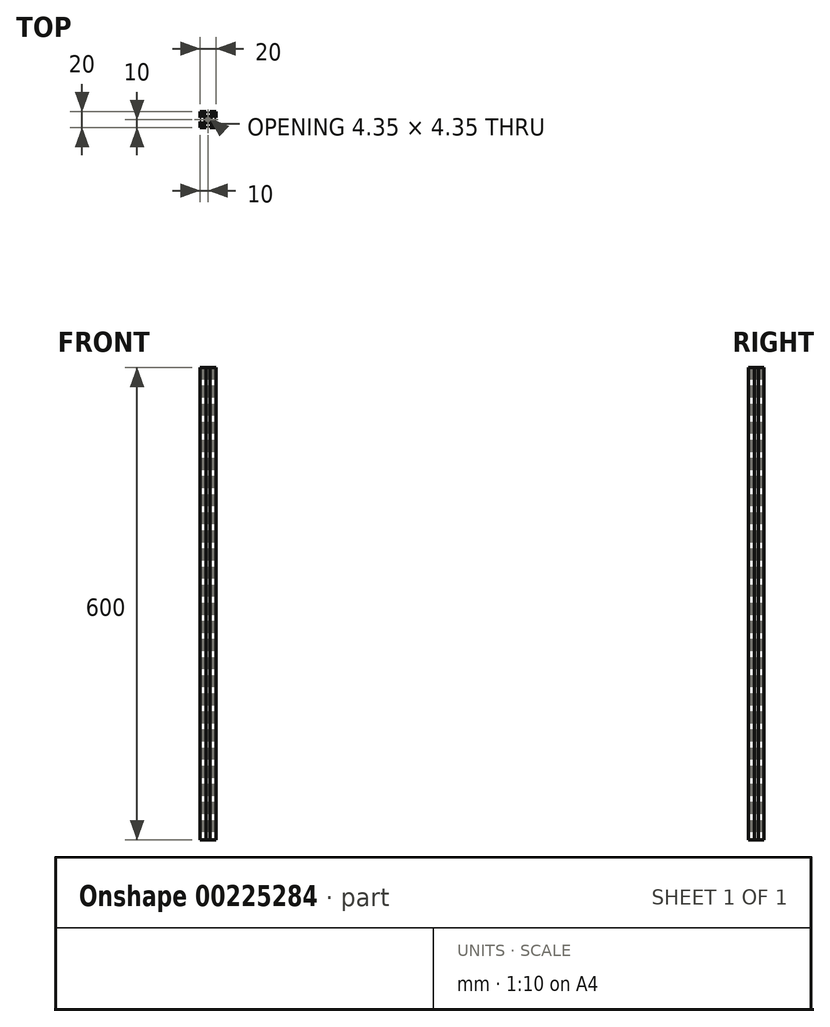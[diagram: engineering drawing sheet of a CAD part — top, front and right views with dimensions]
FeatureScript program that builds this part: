
annotation { "Feature Type Name" : "Feature", "Feature Type Description" : "" }
export const myFeature = defineFeature(function(context is Context, id is Id, definition is map)
    precondition{}
    {
        {
            var Q0;
            Q0=qCreatedBy(makeId("Top.planeOp"),FACE);
            var sketch = newSketch(context, id + "F0", { "sketchPlane" : qUnion([Q0])});
            skLineSegment(sketch, "E0.bottom", {"start": v(10, 10) * mm, "end": v(-10, 10) * mm});
            skLineSegment(sketch, "E0.top", {"start": v(10, -10) * mm, "end": v(-10, -10) * mm});
            skLineSegment(sketch, "E0.left", {"start": v(10, 10) * mm, "end": v(10, -10) * mm});
            skLineSegment(sketch, "E0.right", {"start": v(-10, 10) * mm, "end": v(-10, -10) * mm});
            skPoint(sketch, "E0.middle", {"position": v(0, 0) * mm});
            skLineSegment(sketch, "E1", {"start": v(-10, 10) * mm, "end": v(10, -10) * mm, "construction": true});
            skLineSegment(sketch, "E2", {"start": v(-10, -10) * mm, "end": v(10, 10) * mm, "construction": true});
            skLineSegment(sketch, "E3", {"start": v(0, 10) * mm, "end": v(0, -10) * mm, "construction": true});
            skLineSegment(sketch, "E4", {"start": v(-10, 0) * mm, "end": v(10, 0) * mm, "construction": true});
            skPoint(sketch, "E4.endSnap0", {"position": v(10, 0) * mm});
            skLineSegment(sketch, "E5", {"start": v(-2.63, 13.49) * mm, "end": v(2.63, 13.49) * mm});
            skLineSegment(sketch, "E6", {"start": v(2.63, 13.49) * mm, "end": v(2.63, 8.5) * mm});
            skLineSegment(sketch, "E7", {"start": v(2.63, 8.5) * mm, "end": v(6, 8.5) * mm});
            skLineSegment(sketch, "E8", {"start": v(6, 8.5) * mm, "end": v(6, 7.06) * mm});
            skLineSegment(sketch, "E9", {"start": v(6, 7.06) * mm, "end": v(2.6, 3.66) * mm});
            skLineSegment(sketch, "E10", {"start": v(2.6, 3.66) * mm, "end": v(-2.6, 3.66) * mm});
            skLineSegment(sketch, "E11", {"start": v(-2.6, 3.66) * mm, "end": v(-6, 7.06) * mm});
            skLineSegment(sketch, "E12", {"start": v(-6, 7.06) * mm, "end": v(-6, 8.5) * mm});
            skLineSegment(sketch, "E13", {"start": v(-6, 8.5) * mm, "end": v(-2.63, 8.5) * mm});
            skLineSegment(sketch, "E14", {"start": v(-2.63, 8.5) * mm, "end": v(-2.63, 13.49) * mm});
            skCircle(sketch, "E15", {"center": v(0, 0) * mm, "radius": 2.1 * mm});
            skLineSegment(sketch, "E16.MirrorCS", {"start": v(-7.06, 6) * mm, "end": v(-8.5, 6) * mm});
            skLineSegment(sketch, "E17.MirrorCS", {"start": v(-3.66, 2.6) * mm, "end": v(-7.06, 6) * mm});
            skLineSegment(sketch, "E18.MirrorCS", {"start": v(-8.5, 6) * mm, "end": v(-8.5, 2.63) * mm});
            skLineSegment(sketch, "E19.MirrorCS", {"start": v(-3.66, -2.6) * mm, "end": v(-3.66, 2.6) * mm});
            skLineSegment(sketch, "E20.MirrorCS", {"start": v(-7.06, -6) * mm, "end": v(-3.66, -2.6) * mm});
            skLineSegment(sketch, "E21.MirrorCS", {"start": v(-8.5, -6) * mm, "end": v(-7.06, -6) * mm});
            skLineSegment(sketch, "E22.MirrorCS", {"start": v(-8.5, -2.63) * mm, "end": v(-8.5, -6) * mm});
            skLineSegment(sketch, "E23.MirrorCS", {"start": v(-13.49, -2.63) * mm, "end": v(-8.5, -2.63) * mm});
            skLineSegment(sketch, "E24.MirrorCS", {"start": v(-13.49, 2.63) * mm, "end": v(-13.49, -2.63) * mm});
            skLineSegment(sketch, "E25.MirrorCS", {"start": v(-8.5, 2.63) * mm, "end": v(-13.49, 2.63) * mm});
            skLineSegment(sketch, "E26.MirrorCS", {"start": v(-2.6, -3.66) * mm, "end": v(-6, -7.06) * mm});
            skLineSegment(sketch, "E27.MirrorCS", {"start": v(2.6, -3.66) * mm, "end": v(-2.6, -3.66) * mm});
            skLineSegment(sketch, "E28.MirrorCS", {"start": v(6, -7.06) * mm, "end": v(2.6, -3.66) * mm});
            skLineSegment(sketch, "E29.MirrorCS", {"start": v(6, -8.5) * mm, "end": v(6, -7.06) * mm});
            skLineSegment(sketch, "E30.MirrorCS", {"start": v(2.63, -8.5) * mm, "end": v(6, -8.5) * mm});
            skLineSegment(sketch, "E31.MirrorCS", {"start": v(2.63, -13.49) * mm, "end": v(2.63, -8.5) * mm});
            skLineSegment(sketch, "E32.MirrorCS", {"start": v(-2.63, -13.49) * mm, "end": v(2.63, -13.49) * mm});
            skLineSegment(sketch, "E33.MirrorCS", {"start": v(-2.63, -8.5) * mm, "end": v(-2.63, -13.49) * mm});
            skLineSegment(sketch, "E34.MirrorCS", {"start": v(-6, -8.5) * mm, "end": v(-2.63, -8.5) * mm});
            skLineSegment(sketch, "E35.MirrorCS", {"start": v(-6, -7.06) * mm, "end": v(-6, -8.5) * mm});
            skLineSegment(sketch, "E36.MirrorCS", {"start": v(7.06, 6) * mm, "end": v(3.66, 2.6) * mm});
            skLineSegment(sketch, "E37.MirrorCS", {"start": v(8.5, 6) * mm, "end": v(7.06, 6) * mm});
            skLineSegment(sketch, "E38.MirrorCS", {"start": v(8.5, 2.63) * mm, "end": v(8.5, 6) * mm});
            skLineSegment(sketch, "E39.MirrorCS", {"start": v(13.49, 2.63) * mm, "end": v(8.5, 2.63) * mm});
            skLineSegment(sketch, "E40.MirrorCS", {"start": v(13.49, -2.63) * mm, "end": v(13.49, 2.63) * mm});
            skLineSegment(sketch, "E41.MirrorCS", {"start": v(8.5, -2.63) * mm, "end": v(13.49, -2.63) * mm});
            skLineSegment(sketch, "E42.MirrorCS", {"start": v(8.5, -6) * mm, "end": v(8.5, -2.63) * mm});
            skLineSegment(sketch, "E43.MirrorCS", {"start": v(7.06, -6) * mm, "end": v(8.5, -6) * mm});
            skLineSegment(sketch, "E44.MirrorCS", {"start": v(3.66, -2.6) * mm, "end": v(7.06, -6) * mm});
            skLineSegment(sketch, "E45.MirrorCS", {"start": v(3.66, 2.6) * mm, "end": v(3.66, -2.6) * mm});
            skCircle(sketch, "E46", {"center": v(-1.48, 1.48) * mm, "radius": 0.7 * mm});
            skCircle(sketch, "E47.MirrorC", {"center": v(1.48, 1.48) * mm, "radius": 0.7 * mm});
            skCircle(sketch, "E48.MirrorC", {"center": v(-1.48, -1.48) * mm, "radius": 0.7 * mm});
            skCircle(sketch, "E49.MirrorC", {"center": v(1.48, -1.48) * mm, "radius": 0.7 * mm});
            skSolve(sketch);
        }
        {
            var Q0;
            {var subQ29=sQuery(id+"F0.wireOp",EDGE,"E7");Q0=makeQuery(id+"F0.imprint","IMPRINT",FACE,{"disambiguationData":[TD([[makeQuery(id+"F0.imprint","IMPRINT",EDGE,{"derivedFrom":subQ29}),1.0]])]});}
            extrude(context, id + "F1", {"entities" : qUnion([Q0]), "depth" : 600 * mm});
        }
    });
